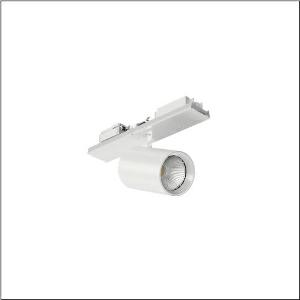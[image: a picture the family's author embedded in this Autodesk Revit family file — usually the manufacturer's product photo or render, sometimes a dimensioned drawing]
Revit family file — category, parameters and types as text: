
# Revit family: licross_r__spot_31_51sl12da45b_e1b3
name_source: partatom
category: Lighting Fixtures
units: mm (PartAtom-declared; Revit-internal decimal feet)

## family parameters
Cut with Voids When Loaded = No
Host = Face
Light Source = No
Part Type = Normal
Room Calculation Point = No
Round Connector Dimension = Use Diameter
Shared = No

## types (1)
- --- (1 x LED, 5140 lm, 43.9 W, 4000K)
    Apparent Load = 44 VA
    CIE Flux Codes = 93 97 99 100 100
    Color Rendering = 90
    Color Temperature = 4000K
    Default Elevation = 1800 mm
    Description = Licross® Spot 31, directional spotlight, light control with lens, of plastic, LED rated luminous flux: 5.140lm, light colour: 940, with plug, 5-pole, mains connection: 220..240V, AC, 50/60Hz, of aluminium, traffic white (RAL 9016), length: 140mm, diameter: 90mm, protection rating (complete): IP20, insulation class (complete): insulation class I (protective earthing), certification: CE, packaging unit: 1 piece
    Height = 175 mm
    Lamp = 1 x LED
    Lamp Light Flux = 5140 lm
    Lamp Power = 43.9 W
    Lamp count = 1
    Length = 90 mm
    Luminous efficacy = 117 lm/W
    Manufacturer = Siteco
    ModVariant = No
    Model = 51SL12DA45B
    Mounting Place = Ceiling
    Mounting Type = Pendant
    Number of Poles = 1
    OnlyDefault = Yes
    Power Factor = 1
    Product Name = Licross® Spot 31
    Product group = directional spotlight
    ProductGroupID = 905
    Protection Class = Protection class I
    Protection Degree = IP 20
    RLX_Detail_Level = 1
    RLX_Emergency_Light_Flux = 0 lm
    RLX_Emergency_Type = 0
    RLX_Emergency_Type_DB = No
    RlxData = <blob elided: 14813 chars, md5=1faa11a8>
    Socket = socket
    Standby Power = 0 W
    System Light Flux = 5140 lm
    System Power = 44 W
    Type Comments = factory setting: luminous flux: 100 % | (ON | ON | ON) | 1050 mA
    Type Image = l_1245720.jpg
    URL = http://relux.com
    VarID = @adj_082019
    Voltage = 0 V
    Weight = 0.00 kg
    Width = 0 mm  [stored 0 ft]

note: [stored X ft] marks values corroborated as IEEE doubles in the binary element streams (Revit-internal decimal feet)

## geometry (parser evidence)
native form markers: Sweep x10
no freeform markers — native parametric forms only
